# Revit family: CFR8
name_source: partatom
category: Lighting Fixtures
revit_build: Autodesk Revit 2014 (Build: 20130308_1515(x64)
units: mm (PartAtom-declared; Revit-internal decimal feet)

## types (1)
- CFR8
    Apparent Load = 27 VA
    Assembly Code = D5020210
    Color Filter = 16777215
    Default Elevation = 22"
    Description = 8'' Horizontal Open,or Wall Wash Downlight
    Dimming Lamp Color Temperature Shift = <None>
    Emit Shape Visible in Rendering = No
    Emit from Circle Diameter = 8"
    Finish = Steel - Hubbell - Gray
    Glass = Hubbell - White Glass
    Housing = Steel - Hubbell - Gray
    Lamp = CFL
    Load Classification = Lighting
    Manufacturer = Prescolite
    Model = CFR8
    Photometric Notes = More IES files download on Photometric Web Link
    Photometric Web File = CFR8126UEB  ST492A1CL.ies
    Photometric Web Link = https://www.hubbell.com
    Power Factor = 0.97
    Product Documentation Link = https://hubbellcdn.com
    Product Page URL = https://www.hubbell.com
    Tilt Angle = -90.00°
    URL = https://www.hubbell.com
    Voltage = 120 V
    Wattage Comments = 18W/26W
    Watts = 26 W

## geometry (parser evidence)
native form markers: Blend x8, Sweep x1
no freeform markers — native parametric forms only
